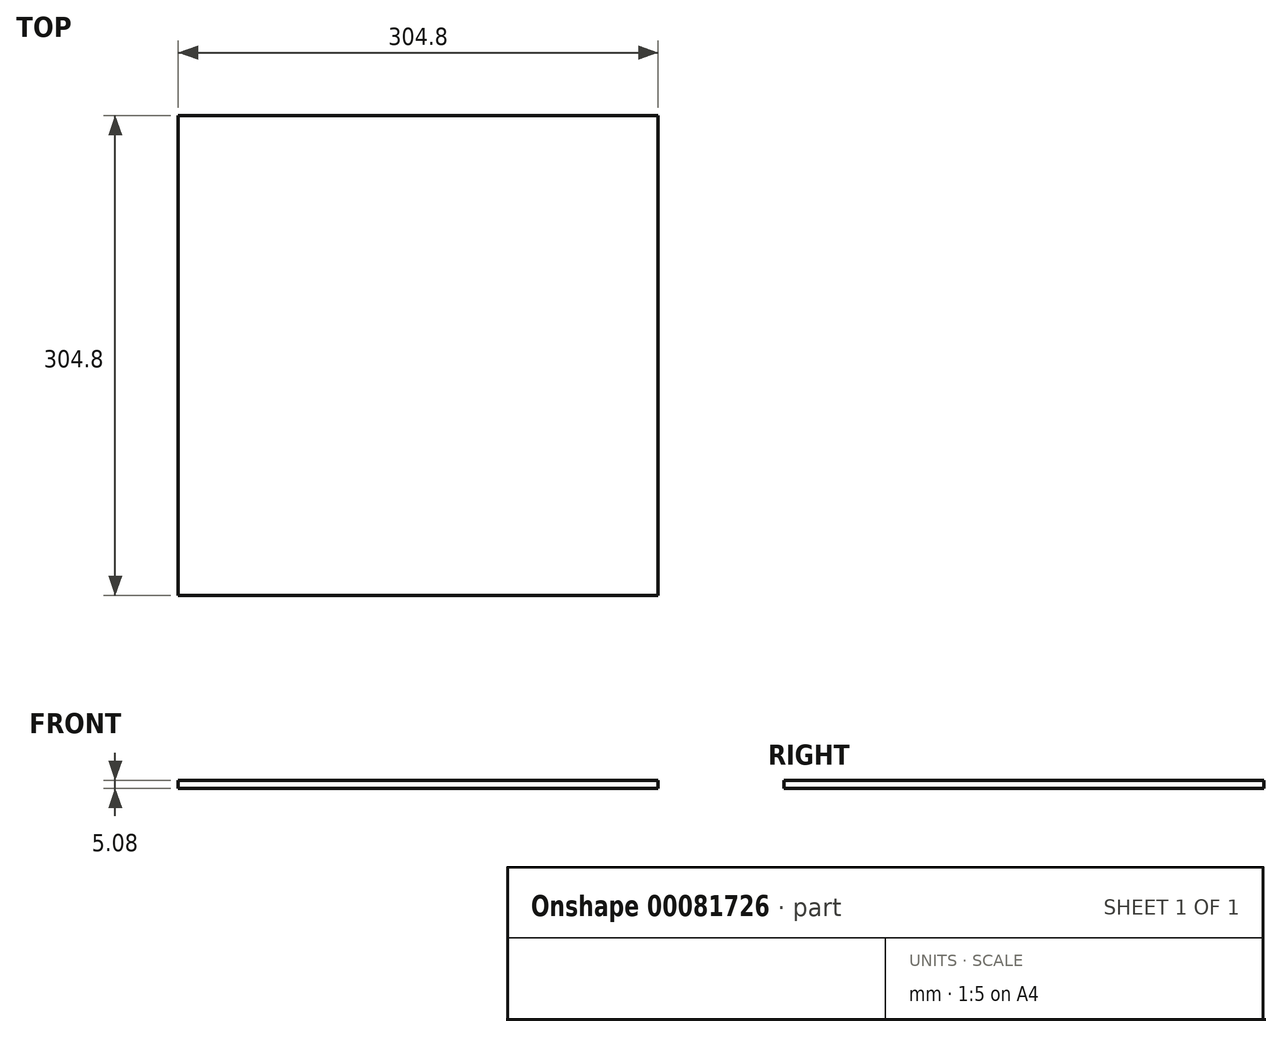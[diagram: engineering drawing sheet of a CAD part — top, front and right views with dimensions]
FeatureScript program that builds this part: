
annotation { "Feature Type Name" : "Feature", "Feature Type Description" : "" }
export const myFeature = defineFeature(function(context is Context, id is Id, definition is map)
    precondition{}
    {
        {
            var Q0;
            Q0=qCreatedBy(makeId("Top.planeOp"),FACE);
            var sketch = newSketch(context, id + "F0", { "sketchPlane" : qUnion([Q0])});
            skLineSegment(sketch, "E0.bottom", {"start": v(152.4, 152.4) * mm, "end": v(-152.4, 152.4) * mm});
            skLineSegment(sketch, "E0.top", {"start": v(152.4, -152.4) * mm, "end": v(-152.4, -152.4) * mm});
            skLineSegment(sketch, "E0.left", {"start": v(152.4, 152.4) * mm, "end": v(152.4, -152.4) * mm});
            skLineSegment(sketch, "E0.right", {"start": v(-152.4, 152.4) * mm, "end": v(-152.4, -152.4) * mm});
            skPoint(sketch, "E0.middle", {"position": v(0, 0) * mm});
            skSolve(sketch);
        }
        {
            var Q0;
            Q0 = qSketchRegion(id + "F0", true);
            extrude(context, id + "F1", {"entities" : qUnion([Q0]), "depth" : 5.08 * mm});
        }
    });
